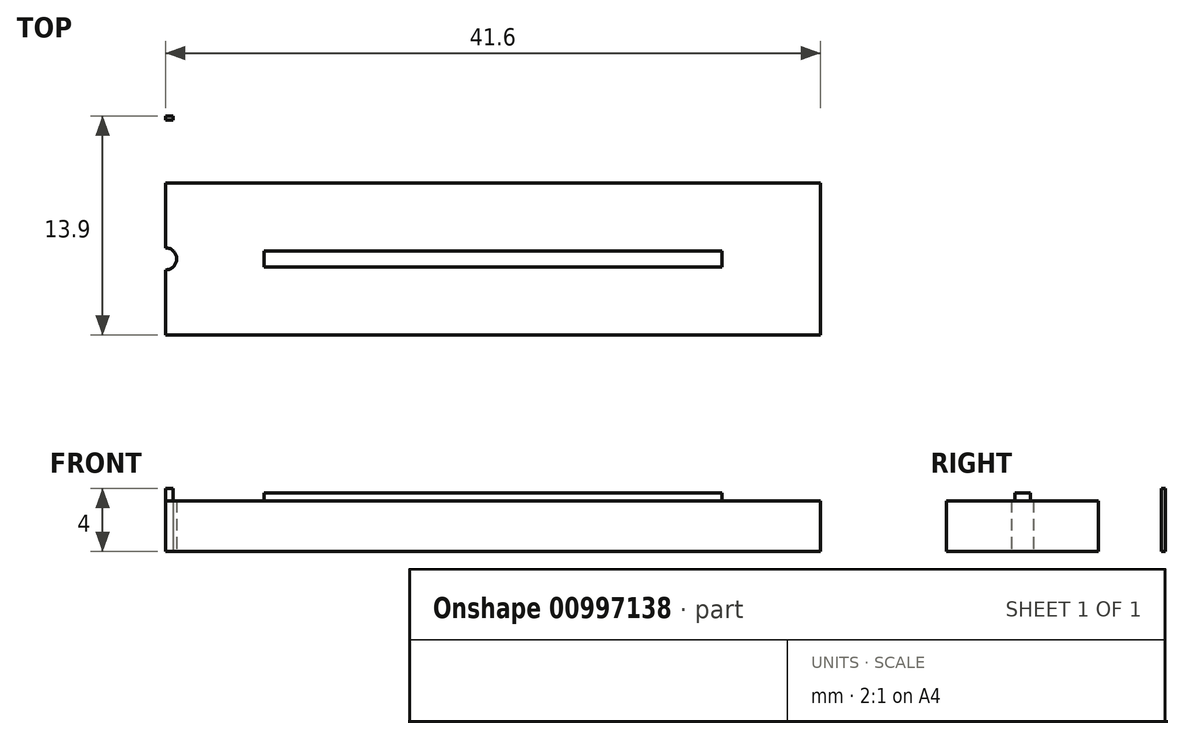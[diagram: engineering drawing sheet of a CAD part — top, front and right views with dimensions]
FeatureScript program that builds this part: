
annotation { "Feature Type Name" : "Feature", "Feature Type Description" : "" }
export const myFeature = defineFeature(function(context is Context, id is Id, definition is map)
    precondition{}
    {
        {
            var Q0;
            Q0=qCreatedBy(makeId("Top.planeOp"),FACE);
            var sketch = newSketch(context, id + "F0", { "sketchPlane" : qUnion([Q0])});
            skLineSegment(sketch, "E0.bottom", {"start": v(-20.8, 4.83) * mm, "end": v(20.8, 4.83) * mm});
            skLineSegment(sketch, "E0.top", {"start": v(-20.8, -4.83) * mm, "end": v(20.8, -4.83) * mm});
            skLineSegment(sketch, "E0.left", {"start": v(-20.8, 4.82) * mm, "end": v(-20.8, -4.82) * mm});
            skLineSegment(sketch, "E0.right", {"start": v(20.8, 4.83) * mm, "end": v(20.8, -4.83) * mm});
            skLineSegment(sketch, "E1", {"start": v(0, 4.82) * mm, "end": v(0, -4.83) * mm, "construction": true});
            skArc(sketch, "E2", {"start": v(-20.8, -0.7) * mm, "mid": v(-20.1, 0) * mm, "end": v(-20.8, 0.7) * mm});
            skSolve(sketch);
        }
        {
            var Q0;
            {var subQ3=sQuery(id+"F0.wireOp",EDGE,"E0.bottom");Q0=makeQuery(id+"F0.imprint","IMPRINT",FACE,{"disambiguationData":[TD([[makeQuery(id+"F0.imprint","IMPRINT",EDGE,{"derivedFrom":subQ3}),-1.0]])]});}
            extrude(context, id + "F1", {"entities" : qUnion([Q0]), "depth" : 3.22 * mm, "offsetDistance" : 25 * mm});
        }
        {
            var Q0;
            Q0=qCreatedBy(makeId("Top.planeOp"),FACE);
            var sketch = newSketch(context, id + "F2", { "sketchPlane" : qUnion([Q0])});
            skLineSegment(sketch, "E3.bottom", {"start": v(-20.8, 9.08) * mm, "end": v(-20.33, 9.08) * mm});
            skLineSegment(sketch, "E3.top", {"start": v(-20.8, 8.83) * mm, "end": v(-20.33, 8.83) * mm});
            skLineSegment(sketch, "E3.left", {"start": v(-20.8, 9.08) * mm, "end": v(-20.8, 8.83) * mm});
            skLineSegment(sketch, "E3.right", {"start": v(-20.33, 9.08) * mm, "end": v(-20.33, 8.83) * mm});
            skSolve(sketch);
        }
        {
            var Q0;
            Q0=makeQuery(id+"F2.imprint","IMPRINT",FACE,{"disambiguationData":[TD([[makeQuery(id+"F2.imprint","IMPRINT",EDGE,{"derivedFrom":sQuery(id+"F2.wireOp",EDGE,"E3.bottom")}),-1.0]])]});
            extrude(context, id + "F3", {"entities" : qUnion([Q0]), "depth" : 4 * mm, "offsetDistance" : 25 * mm});
        }
        {
            var Q0;
            Q0=makeQuery(id+"F1.opExtrude","CAP_FACE",FACE,{"disambiguationData":[OSD([sQuery(id+"F0.wireOp",EDGE,"E0.bottom"),sQuery(id+"F0.wireOp",EDGE,"E0.top"),sQuery(id+"F0.wireOp",EDGE,"E0.left"),sQuery(id+"F0.wireOp",EDGE,"E0.right"),sQuery(id+"F0.wireOp",EDGE,"E2")])],"isStart":false});
            var sketch = newSketch(context, id + "F4", { "sketchPlane" : qUnion([Q0])});
            skLineSegment(sketch, "E4.bottom", {"start": v(-14.55, 0.5) * mm, "end": v(14.55, 0.5) * mm});
            skLineSegment(sketch, "E4.top", {"start": v(-14.55, -0.5) * mm, "end": v(14.55, -0.5) * mm});
            skLineSegment(sketch, "E4.left", {"start": v(-14.55, 0.5) * mm, "end": v(-14.55, -0.5) * mm});
            skLineSegment(sketch, "E4.right", {"start": v(14.55, 0.5) * mm, "end": v(14.55, -0.5) * mm});
            skLineSegment(sketch, "E5", {"start": v(0, -0.5) * mm, "end": v(0, 0.5) * mm, "construction": true});
            skSolve(sketch);
        }
        {
            var Q0;
            Q0=makeQuery(id+"F4.imprint","IMPRINT",FACE,{"disambiguationData":[TD([[makeQuery(id+"F4.imprint","IMPRINT",EDGE,{"derivedFrom":sQuery(id+"F4.wireOp",EDGE,"E4.bottom")}),-1.0]])]});
            extrude(context, id + "F5", {"entities" : qUnion([Q0]), "operationType" : NewBodyOperationType.ADD, "depth" : 0.5 * mm, "offsetDistance" : 25 * mm});
        }
    });
